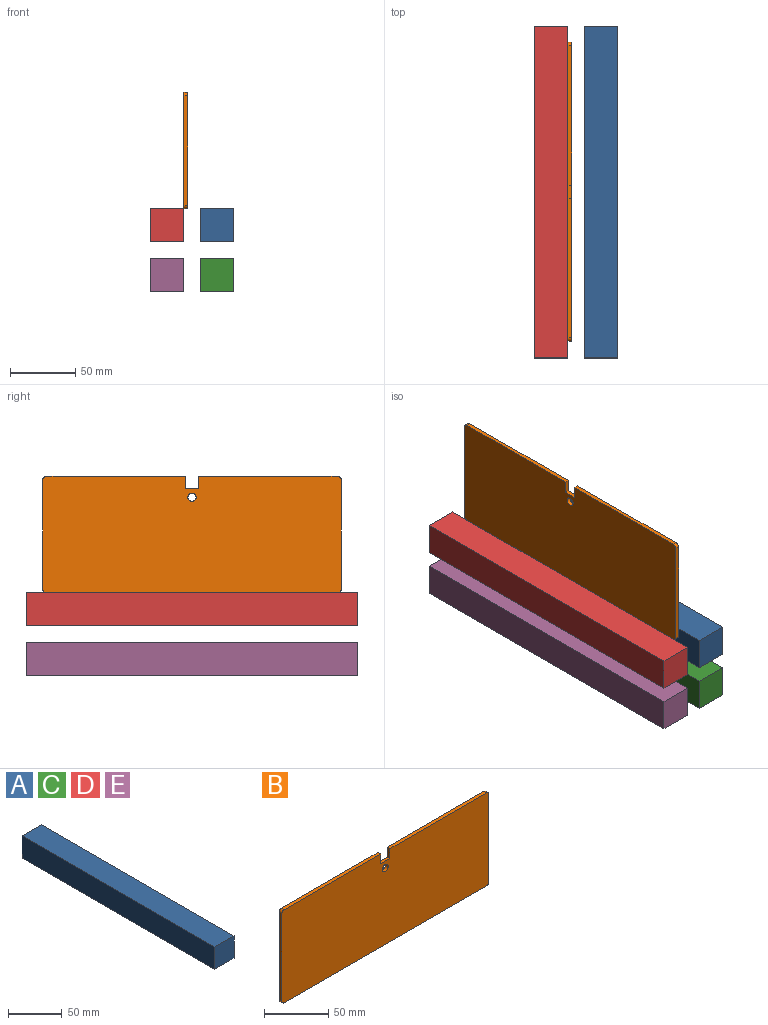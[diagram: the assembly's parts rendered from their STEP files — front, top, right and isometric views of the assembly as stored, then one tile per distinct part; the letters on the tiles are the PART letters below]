
ASSEMBLY  parts=5 mates=3
PART A: 6 faces, bbox 25.4x254x25.4 mm
  f0: plane 254x25.4mm, normal (0,0,1), area 6451.6mm2, adj f1,f3,f4,f5
  f1: plane 254x25.4mm, normal (-1,0,0), area 6451.6mm2, adj f0,f2,f4,f5
  f2: plane 254x25.4mm, normal (0,0,-1), area 6451.6mm2, adj f1,f3,f4,f5
  f3: plane 254x25.4mm, normal (1,0,0), area 6451.6mm2, adj f0,f2,f4,f5
  f4: plane 25.4x25.4mm, normal (0,-1,0), area 645.2mm2, adj f0,f1,f2,f3
  f5: plane 25.4x25.4mm, normal (0,1,0), area 645.2mm2, adj f0,f1,f2,f3
PART B: 15 faces, bbox 228.6x3x88.9 mm
  f0: plane 9.53x3.04mm, normal (1,0,0), area 28.9mm2, adj f1,f11,f12,f13
  f1: plane 106.68x3.04mm, normal (0,0,1), area 324.1mm2, adj f0,f2,f12,f13
  f2: cylinder r=2.54mm len=3.04mm, axis (0,1,0), area 12.1mm2, adj f1,f3,f12,f13
  f3: plane 83.82x3.04mm, normal (-1,0,0), area 254.6mm2, adj f2,f4,f12,f13
  f4: cylinder r=2.54mm len=3.04mm, axis (0,1,0), area 12.1mm2, adj f3,f5,f12,f13
  f5: plane 223.52x3.04mm, normal (0,0,-1), area 679mm2, adj f4,f6,f12,f13
  f6: cylinder r=2.54mm len=3.04mm, axis (0,1,0), area 12.1mm2, adj f5,f7,f12,f13
  f7: plane 83.82x3.04mm, normal (1,0,0), area 254.6mm2, adj f6,f8,f12,f13
  f8: cylinder r=2.54mm len=3.04mm, axis (0,1,0), area 12.1mm2, adj f7,f9,f12,f13
  f9: plane 106.68x3.04mm, normal (0,0,1), area 324.1mm2, adj f8,f10,f12,f13
  f10: plane 9.53x3.04mm, normal (-1,0,0), area 28.9mm2, adj f9,f11,f12,f13
  f11: plane 10.16x3.04mm, normal (0,0,1), area 30.9mm2, adj f0,f10,f12,f13
  f12: plane 228.6x88.9mm, normal (0,-1,0), area 20188.6mm2, adj f0,f1,f2,f3,f4,f5,f6,f7
  f13: plane 228.6x88.9mm, normal (0,1,0), area 20188.6mm2, adj f0,f1,f2,f3,f4,f5,f6,f7
  f14: cylinder r=3.17mm len=6.35mm, axis (0,-1,0), area 60.6mm2, adj f12,f13
PART C: same geometry as A
PART D: same geometry as A
PART E: same geometry as A
PLACE A t=(25.4,0,-12.7)mm
PLACE B rot(axis=(0,0,-1),90deg) t=(1.52,0,88.9)mm
PLACE C t=(25.4,0,-50.8)mm
PLACE D t=(-12.7,0,-12.7)mm
PLACE E t=(-12.7,0,-50.8)mm
MATE fastened B.f12 <-> D.f3  axis (-1,0,0) through (0,0,0)mm
MATE parallel B.f1 <-> D.f0  axis (0,0,1) through (1.52,58.42,88.9)mm
MATE parallel D.f3 <-> B.f13  axis (1,0,0) through (0,0,-12.7)mm
